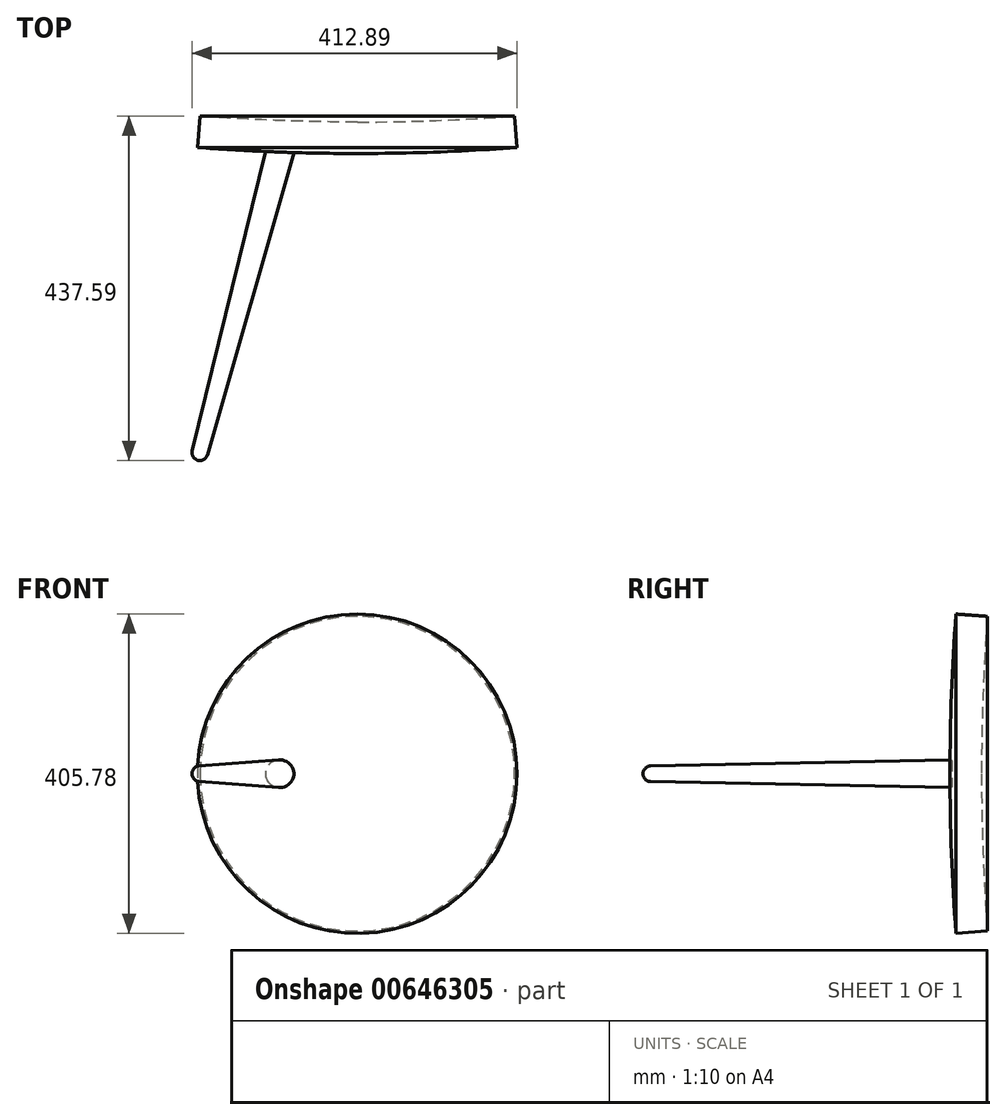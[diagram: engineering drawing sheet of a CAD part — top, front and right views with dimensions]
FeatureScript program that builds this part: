
annotation { "Feature Type Name" : "Feature", "Feature Type Description" : "" }
export const myFeature = defineFeature(function(context is Context, id is Id, definition is map)
    precondition{}
    {
        {
            var Q0;
            Q0=qCreatedBy(makeId("Top.planeOp"),FACE);
            var sketch = newSketch(context, id + "F0", { "sketchPlane" : qUnion([Q0])});
            skArc(sketch, "E0", {"start": v(0, 430) * mm, "mid": v(100, 431.9) * mm, "end": v(199.86, 437.59) * mm});
            skLineSegment(sketch, "E1", {"start": v(0, 0) * mm, "end": v(0, 3065.26) * mm, "construction": true});
            skLineSegment(sketch, "E2", {"start": v(199.86, 437.59) * mm, "end": v(202.89, 397.7) * mm});
            skArc(sketch, "E3.0", {"start": v(0, 390) * mm, "mid": v(101.52, 391.93) * mm, "end": v(202.89, 397.7) * mm});
            skLineSegment(sketch, "E4", {"start": v(0, 430) * mm, "end": v(0, 390) * mm});
            skSolve(sketch);
        }
        {
            var Q0;
            Q0=makeQuery(id+"F0.imprint","IMPRINT",FACE,{"disambiguationData":[TD([[makeQuery(id+"F0.imprint","IMPRINT",EDGE,{"derivedFrom":sQuery(id+"F0.wireOp",EDGE,"E0")}),-1.0]])]});
            var Q1;
            Q1=sQuery(id+"F0.wireOp",EDGE,"E4");
            revolve(context, id + "F1", {"entities" : qUnion([Q0]), "axis" : qUnion([Q1]), "revolveType" : RevolveType.FULL});
        }
        {
            var Q0;
            Q0=qCreatedBy(makeId("Top.planeOp"),FACE);
            var sketch = newSketch(context, id + "F2", { "sketchPlane" : qUnion([Q0])});
            skLineSegment(sketch, "E5", {"start": v(-200, 0) * mm, "end": v(-202.65, 0) * mm});
            skArc(sketch, "E6", {"start": v(-202.57, 0.33) * mm, "mid": v(-195.06, 1.3) * mm, "end": v(-190.39, 7.25) * mm});
            skLineSegment(sketch, "E7", {"start": v(-202.65, 0) * mm, "end": v(-93.84, 410) * mm});
            skLineSegment(sketch, "E8", {"start": v(-93.84, 410) * mm, "end": v(-76.44, 405.38) * mm});
            skLineSegment(sketch, "E9", {"start": v(-76.44, 405.38) * mm, "end": v(-190.39, 7.25) * mm});
            skPoint(sketch, "E10.orphan", {"position": v(0, 0) * mm});
            skSolve(sketch);
        }
        {
            var Q0;
            Q0 = qSketchRegion(id + "F2", true);
            var Q1;
            Q1=sQuery(id+"F2.wireOp",EDGE,"E7");
            revolve(context, id + "F3", {"operationType" : NewBodyOperationType.ADD, "entities" : qUnion([Q0]), "axis" : qUnion([Q1]), "revolveType" : RevolveType.FULL});
        }
    });
